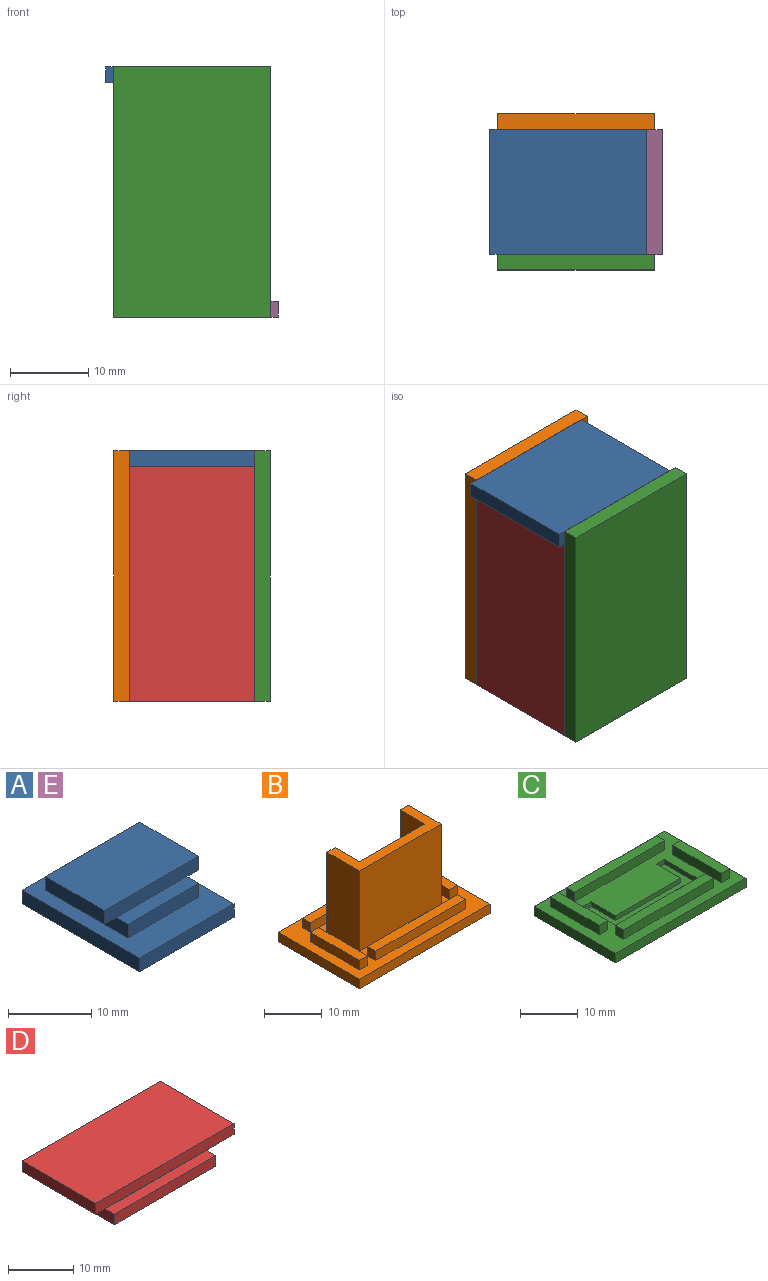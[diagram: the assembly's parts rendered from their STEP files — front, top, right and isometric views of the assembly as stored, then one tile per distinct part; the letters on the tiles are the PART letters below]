
ASSEMBLY  parts=5 mates=4
PART A: 19 faces, bbox 16x20x6 mm
  f0: plane 12x2mm, normal (0,0,1), area 24mm2, adj f7,f9,f10,f13
  f1: plane 20x2mm, normal (1,0,0), area 40mm2, adj f2,f4,f5,f6
  f2: plane 16x2mm, normal (0,1,0), area 32mm2, adj f1,f3,f5,f6
  f3: plane 20x2mm, normal (-1,0,0), area 40mm2, adj f2,f4,f5,f6
  f4: plane 16x2mm, normal (0,-1,0), area 32mm2, adj f1,f3,f5,f6
  f5: plane 20x16mm, normal (0,0,1), area 152mm2, adj f1,f2,f3,f4,f7,f8,f9,f10
  f6: plane 20x16mm, normal (0,0,-1), area 320mm2, adj f1,f2,f3,f4
  f7: plane 14x2mm, normal (-1,0,0), area 28mm2, adj f0,f5,f8,f10,f11,f12
  f8: plane 12x2mm, normal (0,-1,0), area 24mm2, adj f5,f7,f9,f11
  f9: plane 14x2mm, normal (1,0,0), area 28mm2, adj f0,f5,f8,f10,f11,f18
  f10: plane 12x2mm, normal (0,1,0), area 24mm2, adj f0,f5,f7,f9
  f11: plane 12x2mm, normal (0,0,1), area 24mm2, adj f7,f8,f9,f15
  f12: plane 10x2mm, normal (0,0,-1), area 20mm2, adj f7,f13,f14,f15
  f13: plane 16x2mm, normal (0,1,0), area 32mm2, adj f0,f12,f14,f16,f17,f18
  f14: plane 10x2mm, normal (-1,0,0), area 20mm2, adj f12,f13,f15,f17
  f15: plane 16x2mm, normal (0,-1,0), area 32mm2, adj f11,f12,f14,f16,f17,f18
  f16: plane 10x2mm, normal (1,0,0), area 20mm2, adj f13,f15,f17,f18
  f17: plane 16x10mm, normal (0,0,1), area 160mm2, adj f13,f14,f15,f16
  f18: plane 10x2mm, normal (0,0,-1), area 20mm2, adj f9,f13,f15,f16
PART B: 35 faces, bbox 32x20x19 mm
  f0: plane 32x20mm, normal (0,0,1), area 440mm2, adj f1,f2,f3,f4,f6,f7,f8,f9
  f1: plane 20x2mm, normal (1,0,0), area 40mm2, adj f0,f2,f4,f5
  f2: plane 32x2mm, normal (0,1,0), area 64mm2, adj f0,f1,f3,f5
  f3: plane 20x2mm, normal (-1,0,0), area 40mm2, adj f0,f2,f4,f5
  f4: plane 32x2mm, normal (0,-1,0), area 64mm2, adj f0,f1,f3,f5
  f5: plane 32x20mm, normal (0,0,-1), area 640mm2, adj f1,f2,f3,f4
  f6: plane 2x2mm, normal (0,1,0), area 4mm2, adj f0,f7,f9,f10
  f7: plane 12x2mm, normal (-1,0,0), area 24mm2, adj f0,f6,f8,f10
  f8: plane 2x2mm, normal (0,-1,0), area 4mm2, adj f0,f7,f9,f10
  f9: plane 12x2mm, normal (1,0,0), area 24mm2, adj f0,f6,f8,f10
  f10: plane 12x2mm, normal (0,0,1), area 24mm2, adj f6,f7,f8,f9
  f11: plane 2x2mm, normal (0,-1,0), area 4mm2, adj f0,f12,f14,f15
  f12: plane 12x2mm, normal (1,0,0), area 24mm2, adj f0,f11,f13,f15
  f13: plane 2x2mm, normal (0,1,0), area 4mm2, adj f0,f12,f14,f15
  f14: plane 12x2mm, normal (-1,0,0), area 24mm2, adj f0,f11,f13,f15
  f15: plane 12x2mm, normal (0,0,1), area 24mm2, adj f11,f12,f13,f14
  f16: plane 2x2mm, normal (-1,0,0), area 4mm2, adj f0,f17,f19,f20
  f17: plane 22x2mm, normal (0,-1,0), area 44mm2, adj f0,f16,f18,f20
  f18: plane 2x2mm, normal (1,0,0), area 4mm2, adj f0,f17,f19,f20
  f19: plane 22x2mm, normal (0,1,0), area 44mm2, adj f0,f16,f18,f20
  f20: plane 22x2mm, normal (0,0,1), area 44mm2, adj f16,f17,f18,f19
  f21: plane 2x2mm, normal (1,0,0), area 4mm2, adj f0,f22,f24,f25
  f22: plane 22x2mm, normal (0,1,0), area 44mm2, adj f0,f21,f23,f25
  f23: plane 2x2mm, normal (-1,0,0), area 4mm2, adj f0,f22,f24,f25
  f24: plane 22x2mm, normal (0,-1,0), area 44mm2, adj f0,f21,f23,f25
  f25: plane 22x2mm, normal (0,0,1), area 44mm2, adj f21,f22,f23,f24
  f26: plane 17x8mm, normal (-1,0,0), area 136mm2, adj f0,f27,f33,f34
  f27: plane 20x17mm, normal (0,-1,0), area 340mm2, adj f0,f26,f28,f34
  f28: plane 17x8mm, normal (1,0,0), area 136mm2, adj f0,f27,f29,f34
  f29: plane 17x2mm, normal (0,1,0), area 34mm2, adj f0,f28,f30,f34
  f30: plane 17x6mm, normal (-1,0,0), area 102mm2, adj f0,f29,f31,f34
  f31: plane 17x16mm, normal (0,1,0), area 272mm2, adj f0,f30,f32,f34
  f32: plane 17x6mm, normal (1,0,0), area 102mm2, adj f0,f31,f33,f34
  f33: plane 17x2mm, normal (0,1,0), area 34mm2, adj f0,f26,f32,f34
  f34: plane 20x8mm, normal (0,0,1), area 64mm2, adj f26,f27,f28,f29,f30,f31,f32,f33
PART C: 35 faces, bbox 32x20x4 mm
  f0: plane 32x20mm, normal (0,0,1), area 440mm2, adj f1,f2,f3,f4,f6,f7,f8,f9
  f1: plane 20x2mm, normal (1,0,0), area 40mm2, adj f0,f2,f4,f5
  f2: plane 32x2mm, normal (0,1,0), area 64mm2, adj f0,f1,f3,f5
  f3: plane 20x2mm, normal (-1,0,0), area 40mm2, adj f0,f2,f4,f5
  f4: plane 32x2mm, normal (0,-1,0), area 64mm2, adj f0,f1,f3,f5
  f5: plane 32x20mm, normal (0,0,-1), area 640mm2, adj f1,f2,f3,f4
  f6: plane 12x2mm, normal (-1,0,0), area 24mm2, adj f0,f7,f9,f10
  f7: plane 2x2mm, normal (0,-1,0), area 4mm2, adj f0,f6,f8,f10
  f8: plane 12x2mm, normal (1,0,0), area 24mm2, adj f0,f7,f9,f10
  f9: plane 2x2mm, normal (0,1,0), area 4mm2, adj f0,f6,f8,f10
  f10: plane 12x2mm, normal (0,0,1), area 24mm2, adj f6,f7,f8,f9
  f11: plane 12x2mm, normal (1,0,0), area 24mm2, adj f0,f12,f14,f15
  f12: plane 2x2mm, normal (0,1,0), area 4mm2, adj f0,f11,f13,f15
  f13: plane 12x2mm, normal (-1,0,0), area 24mm2, adj f0,f12,f14,f15
  f14: plane 2x2mm, normal (0,-1,0), area 4mm2, adj f0,f11,f13,f15
  f15: plane 12x2mm, normal (0,0,1), area 24mm2, adj f11,f12,f13,f14
  f16: plane 22x2mm, normal (0,-1,0), area 44mm2, adj f0,f17,f19,f20
  f17: plane 2x2mm, normal (1,0,0), area 4mm2, adj f0,f16,f18,f20
  f18: plane 22x2mm, normal (0,1,0), area 44mm2, adj f0,f17,f19,f20
  f19: plane 2x2mm, normal (-1,0,0), area 4mm2, adj f0,f16,f18,f20
  f20: plane 22x2mm, normal (0,0,1), area 44mm2, adj f16,f17,f18,f19
  f21: plane 22x2mm, normal (0,1,0), area 44mm2, adj f0,f22,f24,f25
  f22: plane 2x2mm, normal (-1,0,0), area 4mm2, adj f0,f21,f23,f25
  f23: plane 22x2mm, normal (0,-1,0), area 44mm2, adj f0,f22,f24,f25
  f24: plane 2x2mm, normal (1,0,0), area 4mm2, adj f0,f21,f23,f25
  f25: plane 22x2mm, normal (0,0,1), area 44mm2, adj f21,f22,f23,f24
  f26: plane 2x1mm, normal (0,-1,0), area 2mm2, adj f0,f27,f33,f34
  f27: plane 8x1mm, normal (1,0,0), area 8mm2, adj f0,f26,f28,f34
  f28: plane 20x1mm, normal (0,1,0), area 20mm2, adj f0,f27,f29,f34
  f29: plane 8x1mm, normal (-1,0,0), area 8mm2, adj f0,f28,f30,f34
  f30: plane 2x1mm, normal (0,-1,0), area 2mm2, adj f0,f29,f31,f34
  f31: plane 6x1mm, normal (1,0,0), area 6mm2, adj f0,f30,f32,f34
  f32: plane 16x1mm, normal (0,-1,0), area 16mm2, adj f0,f31,f33,f34
  f33: plane 6x1mm, normal (-1,0,0), area 6mm2, adj f0,f26,f32,f34
  f34: plane 20x8mm, normal (0,0,1), area 64mm2, adj f26,f27,f28,f29,f30,f31,f32,f33
PART D: 19 faces, bbox 30x16x6 mm
  f0: plane 22x2mm, normal (0,0,1), area 44mm2, adj f1,f2,f4,f8
  f1: plane 22x2mm, normal (0,-1,0), area 44mm2, adj f0,f2,f4,f6
  f2: plane 16x2mm, normal (1,0,0), area 32mm2, adj f0,f1,f3,f5,f6,f12
  f3: plane 22x2mm, normal (0,1,0), area 44mm2, adj f2,f4,f5,f6
  f4: plane 16x2mm, normal (-1,0,0), area 32mm2, adj f0,f1,f3,f5,f6,f7
  f5: plane 22x2mm, normal (0,0,1), area 44mm2, adj f2,f3,f4,f10
  f6: plane 22x16mm, normal (0,0,-1), area 352mm2, adj f1,f2,f3,f4
  f7: plane 12x2mm, normal (0,0,-1), area 24mm2, adj f4,f8,f10,f11
  f8: plane 26x2mm, normal (0,-1,0), area 52mm2, adj f0,f7,f9,f11,f12,f18
  f9: plane 12x2mm, normal (1,0,0), area 24mm2, adj f8,f10,f12,f18
  f10: plane 26x2mm, normal (0,1,0), area 52mm2, adj f5,f7,f9,f11,f12,f18
  f11: plane 12x2mm, normal (-1,0,0), area 24mm2, adj f7,f8,f10,f18
  f12: plane 12x2mm, normal (0,0,-1), area 24mm2, adj f2,f8,f9,f10
  f13: plane 16x2mm, normal (1,0,0), area 32mm2, adj f14,f16,f17,f18
  f14: plane 30x2mm, normal (0,1,0), area 60mm2, adj f13,f15,f17,f18
  f15: plane 16x2mm, normal (-1,0,0), area 32mm2, adj f14,f16,f17,f18
  f16: plane 30x2mm, normal (0,-1,0), area 60mm2, adj f13,f15,f17,f18
  f17: plane 30x16mm, normal (0,0,1), area 480mm2, adj f13,f14,f15,f16
  f18: plane 30x16mm, normal (0,0,-1), area 168mm2, adj f8,f9,f10,f11,f13,f14,f15,f16
PART E: same geometry as A
PLACE A rot(axis=(0.71,-0.71,0),180deg) t=(-5,0.5,16)mm
PLACE B rot(axis=(0.58,-0.58,0.58),120deg) t=(-4,10.5,0)mm
PLACE C rot(axis=(-0.58,0.58,0.58),120deg) t=(-4,-9.5,0)mm
PLACE D rot(axis=(0,-1,0),90deg) t=(-8,0.5,-1)mm
PLACE E rot(axis=(0,0,-1),90deg) t=(-3,0.5,-16)mm
MATE fastened C.f34 <-> B.f34  axis (0,1,0) through (0,-8.5,-10)mm
MATE fastened A.f9 <-> C.f10  axis (0,-1,0) through (-6,-5.5,13)mm
MATE fastened C.f20 <-> D.f8  axis (0,1,0) through (-11,-5.5,-1)mm
MATE fastened E.f9 <-> C.f15  axis (0,-1,0) through (-2,-5.5,-13)mm
